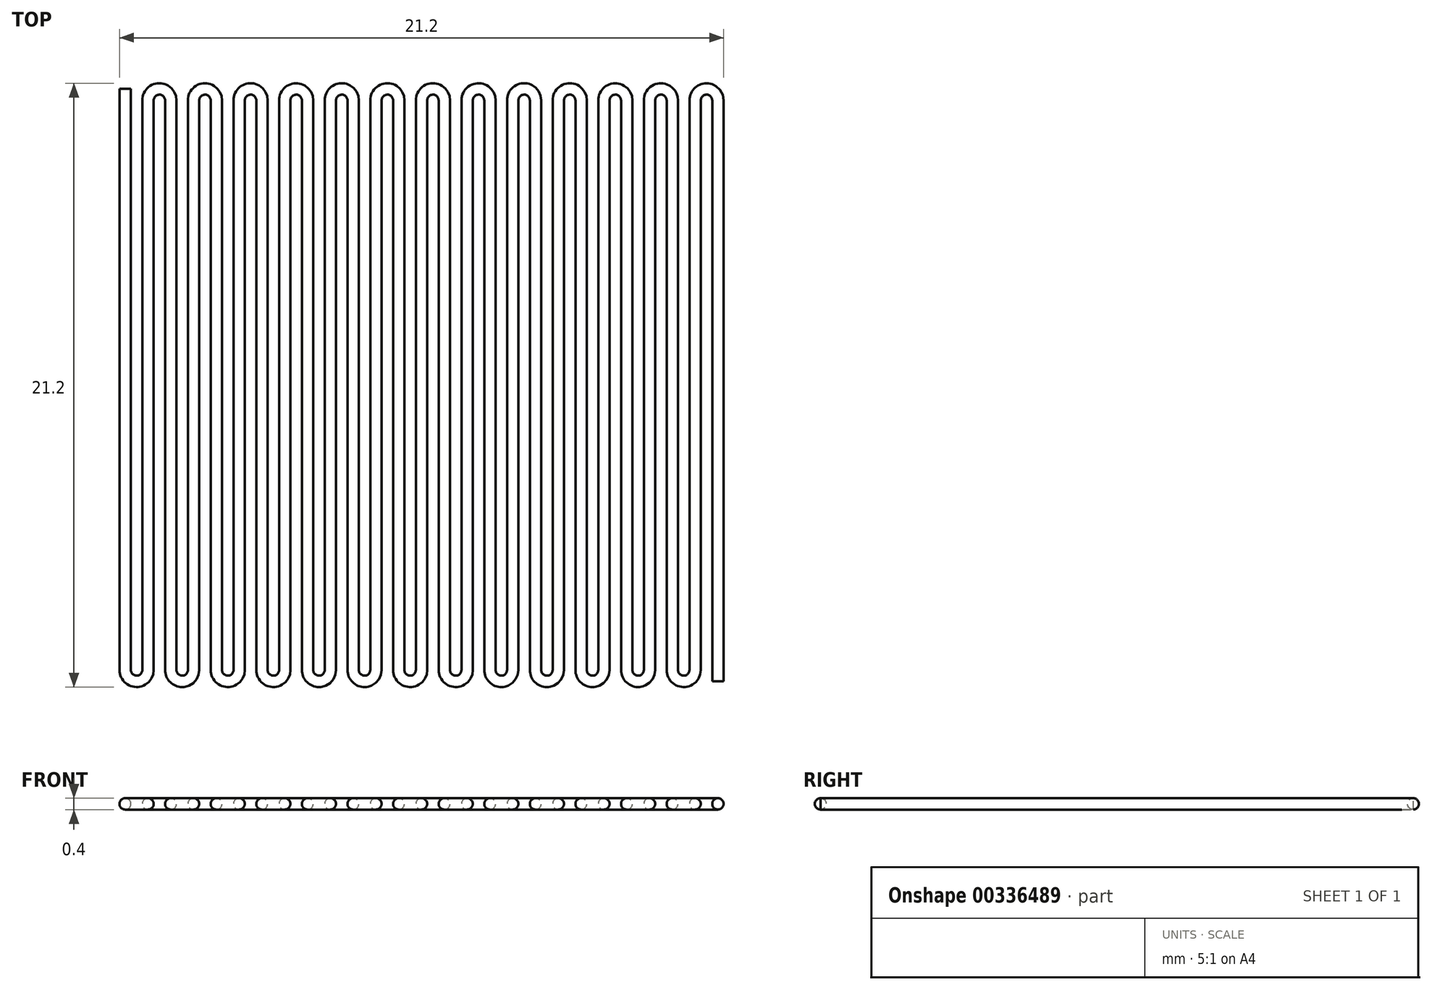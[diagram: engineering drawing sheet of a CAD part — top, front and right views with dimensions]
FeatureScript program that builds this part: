
annotation { "Feature Type Name" : "Feature", "Feature Type Description" : "" }
export const myFeature = defineFeature(function(context is Context, id is Id, definition is map)
    precondition{}
    {
        {
            var Q0;
            Q0=qCreatedBy(makeId("Top.planeOp"),FACE);
            cPlane(context, id + "F0", {"entities" : qUnion([Q0]), "cplaneType" : CPlaneType.OFFSET, "offset" : 0.2 * mm, "width" : 150 * mm, "height" : 150 * mm});
        }
        {
            var Q0;
            Q0=qCreatedBy(id+"F0.planeOp",FACE);
            var sketch = newSketch(context, id + "F1", { "sketchPlane" : qUnion([Q0])});
            skLineSegment(sketch, "E0.bottom", {"start": v(10.4, 10.4) * mm, "end": v(-10.4, 10.4) * mm});
            skLineSegment(sketch, "E0.top", {"start": v(10.4, -10.4) * mm, "end": v(-10.4, -10.4) * mm});
            skLineSegment(sketch, "E0.left", {"start": v(10.4, 10) * mm, "end": v(10.4, -10.4) * mm});
            skLineSegment(sketch, "E0.right", {"start": v(-10.4, 10.4) * mm, "end": v(-10.4, -10.4) * mm});
            skPoint(sketch, "E0.middle", {"position": v(0, 0) * mm});
            skLineSegment(sketch, "E1", {"start": v(9.6, 10) * mm, "end": v(9.6, -10) * mm});
            skLineSegment(sketch, "E2", {"start": v(8.8, 10.4) * mm, "end": v(8.8, -10) * mm});
            skLineSegment(sketch, "E3", {"start": v(10.4, 10) * mm, "end": v(10.4, -10) * mm});
            skLineSegment(sketch, "E4", {"start": v(8.8, -10) * mm, "end": v(8.8, 10) * mm});
            skLineSegment(sketch, "E5", {"start": v(10.4, 10.4) * mm, "end": v(10.4, -10.4) * mm});
            skArc(sketch, "E6", {"start": v(9.6, 10) * mm, "mid": v(10, 10.4) * mm, "end": v(10.4, 10) * mm});
            skArc(sketch, "E7", {"start": v(8.8, -10) * mm, "mid": v(9.2, -10.4) * mm, "end": v(9.6, -10) * mm});
            skLineSegment(sketch, "E8.1.0.0", {"start": v(8.8, 10) * mm, "end": v(8.8, -10) * mm});
            skArc(sketch, "E8.1.0.1", {"start": v(8, 10) * mm, "mid": v(8.4, 10.4) * mm, "end": v(8.8, 10) * mm});
            skLineSegment(sketch, "E8.1.0.2", {"start": v(8, 10) * mm, "end": v(8, -10) * mm});
            skArc(sketch, "E8.1.0.3", {"start": v(7.2, -10) * mm, "mid": v(7.6, -10.4) * mm, "end": v(8, -10) * mm});
            skLineSegment(sketch, "E8.1.0.4", {"start": v(7.2, -10) * mm, "end": v(7.2, 10) * mm});
            skLineSegment(sketch, "E8.2.0.0", {"start": v(7.2, 10) * mm, "end": v(7.2, -10) * mm});
            skArc(sketch, "E8.2.0.1", {"start": v(6.4, 10) * mm, "mid": v(6.8, 10.4) * mm, "end": v(7.2, 10) * mm});
            skLineSegment(sketch, "E8.2.0.2", {"start": v(6.4, 10) * mm, "end": v(6.4, -10) * mm});
            skArc(sketch, "E8.2.0.3", {"start": v(5.6, -10) * mm, "mid": v(6, -10.4) * mm, "end": v(6.4, -10) * mm});
            skLineSegment(sketch, "E8.2.0.4", {"start": v(5.6, -10) * mm, "end": v(5.6, 10) * mm});
            skLineSegment(sketch, "E8.3.0.0", {"start": v(5.6, 10) * mm, "end": v(5.6, -10) * mm});
            skArc(sketch, "E8.3.0.1", {"start": v(4.8, 10) * mm, "mid": v(5.2, 10.4) * mm, "end": v(5.6, 10) * mm});
            skLineSegment(sketch, "E8.3.0.2", {"start": v(4.8, 10) * mm, "end": v(4.8, -10) * mm});
            skArc(sketch, "E8.3.0.3", {"start": v(4, -10) * mm, "mid": v(4.4, -10.4) * mm, "end": v(4.8, -10) * mm});
            skLineSegment(sketch, "E8.3.0.4", {"start": v(4, -10) * mm, "end": v(4, 10) * mm});
            skLineSegment(sketch, "E8.4.0.0", {"start": v(4, 10) * mm, "end": v(4, -10) * mm});
            skArc(sketch, "E8.4.0.1", {"start": v(3.2, 10) * mm, "mid": v(3.6, 10.4) * mm, "end": v(4, 10) * mm});
            skLineSegment(sketch, "E8.4.0.2", {"start": v(3.2, 10) * mm, "end": v(3.2, -10) * mm});
            skArc(sketch, "E8.4.0.3", {"start": v(2.4, -10) * mm, "mid": v(2.8, -10.4) * mm, "end": v(3.2, -10) * mm});
            skLineSegment(sketch, "E8.4.0.4", {"start": v(2.4, -10) * mm, "end": v(2.4, 10) * mm});
            skLineSegment(sketch, "E8.5.0.0", {"start": v(2.4, 10) * mm, "end": v(2.4, -10) * mm});
            skArc(sketch, "E8.5.0.1", {"start": v(1.6, 10) * mm, "mid": v(2, 10.4) * mm, "end": v(2.4, 10) * mm});
            skLineSegment(sketch, "E8.5.0.2", {"start": v(1.6, 10) * mm, "end": v(1.6, -10) * mm});
            skArc(sketch, "E8.5.0.3", {"start": v(0.8, -10) * mm, "mid": v(1.2, -10.4) * mm, "end": v(1.6, -10) * mm});
            skLineSegment(sketch, "E8.5.0.4", {"start": v(0.8, -10) * mm, "end": v(0.8, 10) * mm});
            skLineSegment(sketch, "E8.6.0.0", {"start": v(0.8, 10) * mm, "end": v(0.8, -10) * mm});
            skArc(sketch, "E8.6.0.1", {"start": v(0, 10) * mm, "mid": v(0.4, 10.4) * mm, "end": v(0.8, 10) * mm});
            skLineSegment(sketch, "E8.6.0.2", {"start": v(0, 10) * mm, "end": v(0, -10) * mm});
            skArc(sketch, "E8.6.0.3", {"start": v(-0.8, -10) * mm, "mid": v(-0.4, -10.4) * mm, "end": v(0, -10) * mm});
            skLineSegment(sketch, "E8.6.0.4", {"start": v(-0.8, -10) * mm, "end": v(-0.8, 10) * mm});
            skLineSegment(sketch, "E8.7.0.0", {"start": v(-0.8, 10) * mm, "end": v(-0.8, -10) * mm});
            skArc(sketch, "E8.7.0.1", {"start": v(-1.6, 10) * mm, "mid": v(-1.2, 10.4) * mm, "end": v(-0.8, 10) * mm});
            skLineSegment(sketch, "E8.7.0.2", {"start": v(-1.6, 10) * mm, "end": v(-1.6, -10) * mm});
            skArc(sketch, "E8.7.0.3", {"start": v(-2.4, -10) * mm, "mid": v(-2, -10.4) * mm, "end": v(-1.6, -10) * mm});
            skLineSegment(sketch, "E8.7.0.4", {"start": v(-2.4, -10) * mm, "end": v(-2.4, 10) * mm});
            skLineSegment(sketch, "E8.8.0.0", {"start": v(-2.4, 10) * mm, "end": v(-2.4, -10) * mm});
            skArc(sketch, "E8.8.0.1", {"start": v(-3.2, 10) * mm, "mid": v(-2.8, 10.4) * mm, "end": v(-2.4, 10) * mm});
            skLineSegment(sketch, "E8.8.0.2", {"start": v(-3.2, 10) * mm, "end": v(-3.2, -10) * mm});
            skArc(sketch, "E8.8.0.3", {"start": v(-4, -10) * mm, "mid": v(-3.6, -10.4) * mm, "end": v(-3.2, -10) * mm});
            skLineSegment(sketch, "E8.8.0.4", {"start": v(-4, -10) * mm, "end": v(-4, 10) * mm});
            skLineSegment(sketch, "E8.9.0.0", {"start": v(-4, 10) * mm, "end": v(-4, -10) * mm});
            skArc(sketch, "E8.9.0.1", {"start": v(-4.8, 10) * mm, "mid": v(-4.4, 10.4) * mm, "end": v(-4, 10) * mm});
            skLineSegment(sketch, "E8.9.0.2", {"start": v(-4.8, 10) * mm, "end": v(-4.8, -10) * mm});
            skArc(sketch, "E8.9.0.3", {"start": v(-5.6, -10) * mm, "mid": v(-5.2, -10.4) * mm, "end": v(-4.8, -10) * mm});
            skLineSegment(sketch, "E8.9.0.4", {"start": v(-5.6, -10) * mm, "end": v(-5.6, 10) * mm});
            skLineSegment(sketch, "E8.10.0.0", {"start": v(-5.6, 10) * mm, "end": v(-5.6, -10) * mm});
            skArc(sketch, "E8.10.0.1", {"start": v(-6.4, 10) * mm, "mid": v(-6, 10.4) * mm, "end": v(-5.6, 10) * mm});
            skLineSegment(sketch, "E8.10.0.2", {"start": v(-6.4, 10) * mm, "end": v(-6.4, -10) * mm});
            skArc(sketch, "E8.10.0.3", {"start": v(-7.2, -10) * mm, "mid": v(-6.8, -10.4) * mm, "end": v(-6.4, -10) * mm});
            skLineSegment(sketch, "E8.10.0.4", {"start": v(-7.2, -10) * mm, "end": v(-7.2, 10) * mm});
            skLineSegment(sketch, "E8.11.0.0", {"start": v(-7.2, 10) * mm, "end": v(-7.2, -10) * mm});
            skArc(sketch, "E8.11.0.1", {"start": v(-8, 10) * mm, "mid": v(-7.6, 10.4) * mm, "end": v(-7.2, 10) * mm});
            skLineSegment(sketch, "E8.11.0.2", {"start": v(-8, 10) * mm, "end": v(-8, -10) * mm});
            skArc(sketch, "E8.11.0.3", {"start": v(-8.8, -10) * mm, "mid": v(-8.4, -10.4) * mm, "end": v(-8, -10) * mm});
            skLineSegment(sketch, "E8.11.0.4", {"start": v(-8.8, -10) * mm, "end": v(-8.8, 10) * mm});
            skLineSegment(sketch, "E8.12.0.0", {"start": v(-8.8, 10) * mm, "end": v(-8.8, -10) * mm});
            skArc(sketch, "E8.12.0.1", {"start": v(-9.6, 10) * mm, "mid": v(-9.2, 10.4) * mm, "end": v(-8.8, 10) * mm});
            skLineSegment(sketch, "E8.12.0.2", {"start": v(-9.6, 10) * mm, "end": v(-9.6, -10) * mm});
            skArc(sketch, "E8.12.0.3", {"start": v(-10.4, -10) * mm, "mid": v(-10, -10.4) * mm, "end": v(-9.6, -10) * mm});
            skLineSegment(sketch, "E8.12.0.4", {"start": v(-10.4, -10) * mm, "end": v(-10.4, 10) * mm});
            skLineSegment(sketch, "E8.direction1", {"start": v(8.8, -10) * mm, "end": v(7.2, -10) * mm, "construction": true});
            skLineSegment(sketch, "E9", {"start": v(-10.4, -10) * mm, "end": v(-10.4, 10.4) * mm});
            skSolve(sketch);
        }
        {
            var Q0;
            Q0=sQuery(id+"F1.wireOp",EDGE,"E5");
            var Q1;
            Q1=sQuery(id+"F1.wireOp",VERTEX,"E5.end");
            cPlane(context, id + "F2", {"entities" : qUnion([Q0, Q1]), "cplaneType" : CPlaneType.LINE_POINT, "offset" : 25 * mm, "width" : 150 * mm, "height" : 150 * mm});
        }
        {
            var Q0;
            Q0=qCreatedBy(id+"F2.planeOp",FACE);
            var sketch = newSketch(context, id + "F3", { "sketchPlane" : qUnion([Q0])});
            skCircle(sketch, "E10", {"center": v(10.4, 0.2) * mm, "radius": 0.2 * mm});
            skSolve(sketch);
        }
        {
            var Q0;
            Q0=makeQuery(id+"F3.imprint","IMPRINT",FACE,{"disambiguationData":[TD([[makeQuery(id+"F3.imprint","IMPRINT",EDGE,{"derivedFrom":sQuery(id+"F3.wireOp",EDGE,"E10")}),1.0]])]});
            var Q1;
            Q1=sQuery(id+"F1.wireOp",EDGE,"E0.left");
            var Q2;
            Q2=sQuery(id+"F1.wireOp",EDGE,"E6");
            var Q3;
            Q3=sQuery(id+"F1.wireOp",EDGE,"E1");
            var Q4;
            Q4=sQuery(id+"F1.wireOp",EDGE,"E7");
            var Q5;
            Q5=sQuery(id+"F1.wireOp",EDGE,"E8.1.0.0");
            var Q6;
            Q6=sQuery(id+"F1.wireOp",EDGE,"E8.1.0.2");
            var Q7;
            Q7=sQuery(id+"F1.wireOp",EDGE,"E8.1.0.3");
            var Q8;
            Q8=sQuery(id+"F1.wireOp",EDGE,"E8.2.0.0");
            var Q9;
            Q9=sQuery(id+"F1.wireOp",EDGE,"E8.2.0.2");
            var Q10;
            Q10=sQuery(id+"F1.wireOp",EDGE,"E8.2.0.3");
            var Q11;
            Q11=sQuery(id+"F1.wireOp",EDGE,"E8.3.0.0");
            var Q12;
            Q12=sQuery(id+"F1.wireOp",EDGE,"E8.2.0.1");
            var Q13;
            Q13=sQuery(id+"F1.wireOp",EDGE,"E8.1.0.1");
            var Q14;
            Q14=sQuery(id+"F1.wireOp",EDGE,"E8.3.0.1");
            var Q15;
            Q15=sQuery(id+"F1.wireOp",EDGE,"E8.3.0.2");
            var Q16;
            Q16=sQuery(id+"F1.wireOp",EDGE,"E8.3.0.3");
            var Q17;
            Q17=sQuery(id+"F1.wireOp",EDGE,"E8.3.0.4");
            var Q18;
            Q18=sQuery(id+"F1.wireOp",EDGE,"E8.4.0.1");
            var Q19;
            Q19=sQuery(id+"F1.wireOp",EDGE,"E8.4.0.2");
            var Q20;
            Q20=sQuery(id+"F1.wireOp",EDGE,"E8.5.0.0");
            var Q21;
            Q21=sQuery(id+"F1.wireOp",EDGE,"E8.6.0.0");
            var Q22;
            Q22=sQuery(id+"F1.wireOp",EDGE,"E8.6.0.2");
            var Q23;
            Q23=sQuery(id+"F1.wireOp",EDGE,"E8.5.0.2");
            var Q24;
            Q24=sQuery(id+"F1.wireOp",EDGE,"E8.5.0.1");
            var Q25;
            Q25=sQuery(id+"F1.wireOp",EDGE,"E8.6.0.1");
            var Q26;
            Q26=sQuery(id+"F1.wireOp",EDGE,"E8.5.0.2");
            var Q27;
            Q27=sQuery(id+"F1.wireOp",EDGE,"E8.4.0.3");
            var Q28;
            Q28=sQuery(id+"F1.wireOp",EDGE,"E8.5.0.3");
            var Q29;
            Q29=sQuery(id+"F1.wireOp",EDGE,"E8.6.0.3");
            var Q30;
            Q30=sQuery(id+"F1.wireOp",EDGE,"E8.7.0.0");
            var Q31;
            Q31=sQuery(id+"F1.wireOp",EDGE,"E8.7.0.2");
            var Q32;
            Q32=sQuery(id+"F1.wireOp",EDGE,"E8.7.0.3");
            var Q33;
            Q33=sQuery(id+"F1.wireOp",EDGE,"E8.8.0.0");
            var Q34;
            Q34=sQuery(id+"F1.wireOp",EDGE,"E8.8.0.2");
            var Q35;
            Q35=sQuery(id+"F1.wireOp",EDGE,"E8.8.0.3");
            var Q36;
            Q36=sQuery(id+"F1.wireOp",EDGE,"E8.8.0.4");
            var Q37;
            Q37=sQuery(id+"F1.wireOp",EDGE,"E8.9.0.2");
            var Q38;
            Q38=sQuery(id+"F1.wireOp",EDGE,"E8.9.0.3");
            var Q39;
            Q39=sQuery(id+"F1.wireOp",EDGE,"E8.10.0.0");
            var Q40;
            Q40=sQuery(id+"F1.wireOp",EDGE,"E8.10.0.2");
            var Q41;
            Q41=sQuery(id+"F1.wireOp",EDGE,"E8.10.0.3");
            var Q42;
            Q42=sQuery(id+"F1.wireOp",EDGE,"E8.10.0.4");
            var Q43;
            Q43=sQuery(id+"F1.wireOp",EDGE,"E8.10.0.1");
            var Q44;
            Q44=sQuery(id+"F1.wireOp",EDGE,"E8.9.0.1");
            var Q45;
            Q45=sQuery(id+"F1.wireOp",EDGE,"E8.8.0.1");
            var Q46;
            Q46=sQuery(id+"F1.wireOp",EDGE,"E8.7.0.1");
            var Q47;
            Q47=sQuery(id+"F1.wireOp",EDGE,"E8.11.0.1");
            var Q48;
            Q48=sQuery(id+"F1.wireOp",EDGE,"E8.11.0.2");
            var Q49;
            Q49=sQuery(id+"F1.wireOp",EDGE,"E8.11.0.3");
            var Q50;
            Q50=sQuery(id+"F1.wireOp",EDGE,"E8.12.0.0");
            var Q51;
            Q51=sQuery(id+"F1.wireOp",EDGE,"E8.12.0.2");
            var Q52;
            Q52=sQuery(id+"F1.wireOp",EDGE,"E8.12.0.3");
            var Q53;
            Q53=sQuery(id+"F1.wireOp",EDGE,"E8.12.0.1");
            var Q54;
            Q54=sQuery(id+"F1.wireOp",EDGE,"E9");
            sweep(context, id + "F4", {"profiles" : qUnion([Q0]), "path" : qUnion([Q1, Q2, Q3, Q4, Q5, Q6, Q7, Q8, Q9, Q10, Q11, Q12, Q13, Q14, Q15, Q16, Q17, Q18, Q19, Q20, Q21, Q22, Q23, Q24, Q25, Q26, Q27, Q28, Q29, Q30, Q31, Q32, Q33, Q34, Q35, Q36, Q37, Q38, Q39, Q40, Q41, Q42, Q43, Q44, Q45, Q46, Q47, Q48, Q49, Q50, Q51, Q52, Q53, Q54])});
        }
        {
            var Q0;
            Q0=qCreatedBy(id+"F0.planeOp",FACE);
            cPlane(context, id + "F5", {"entities" : qUnion([Q0]), "cplaneType" : CPlaneType.OFFSET, "offset" : 0.4 * mm, "width" : 150 * mm, "height" : 150 * mm});
        }
    });
